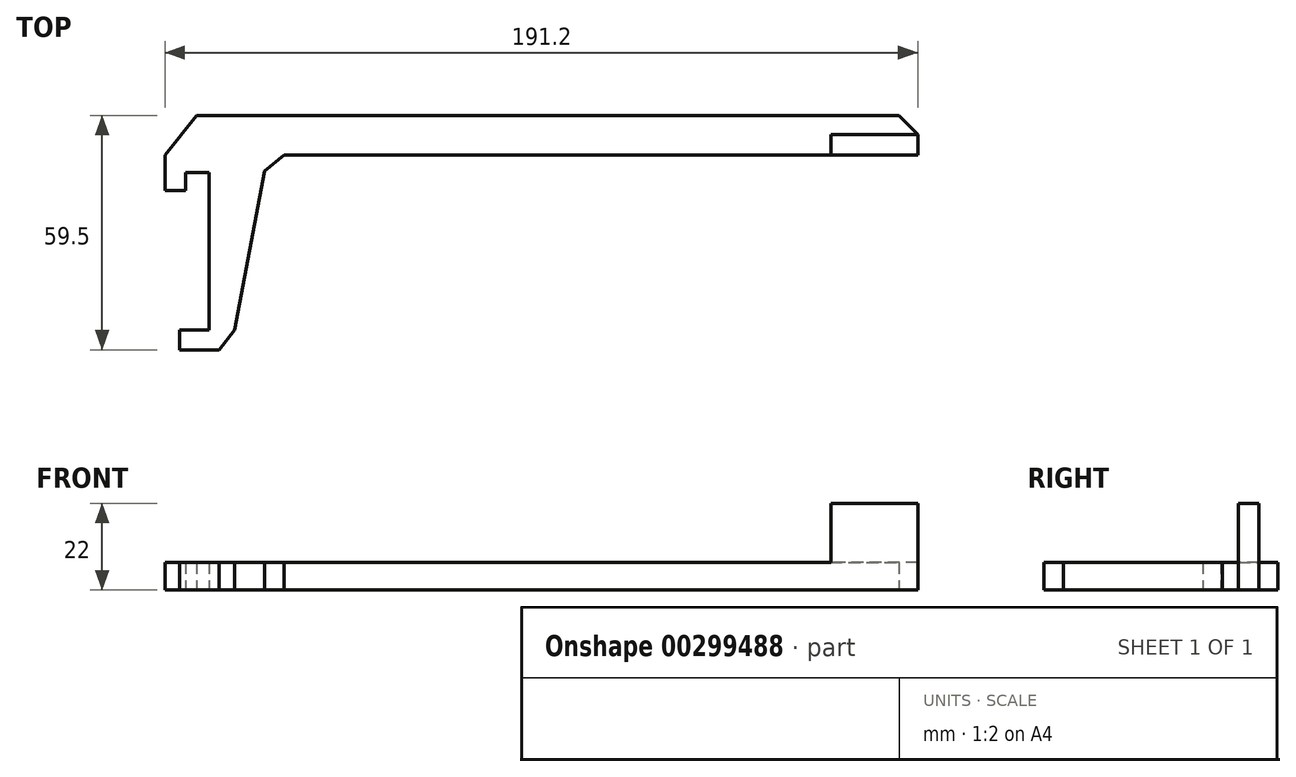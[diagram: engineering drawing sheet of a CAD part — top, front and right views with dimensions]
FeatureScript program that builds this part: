
annotation { "Feature Type Name" : "Feature", "Feature Type Description" : "" }
export const myFeature = defineFeature(function(context is Context, id is Id, definition is map)
    precondition{}
    {
        {
            var Q0;
            Q0=qCreatedBy(makeId("Top.planeOp"),FACE);
            var sketch = newSketch(context, id + "F0", { "sketchPlane" : qUnion([Q0])});
            skLineSegment(sketch, "E0", {"start": v(-18.72, 27.02) * mm, "end": v(-12.72, 27.02) * mm});
            skLineSegment(sketch, "E1", {"start": v(-12.72, 27.02) * mm, "end": v(-12.72, -12.98) * mm});
            skLineSegment(sketch, "E2", {"start": v(-12.72, -12.98) * mm, "end": v(-20.22, -12.98) * mm});
            skLineSegment(sketch, "E3", {"start": v(-20.22, -12.98) * mm, "end": v(-20.22, -17.98) * mm});
            skLineSegment(sketch, "E4", {"start": v(-20.22, -17.98) * mm, "end": v(-10.22, -17.98) * mm});
            skLineSegment(sketch, "E5", {"start": v(-10.22, -17.98) * mm, "end": v(-6.22, -12.98) * mm});
            skLineSegment(sketch, "E6", {"start": v(-18.72, 27.02) * mm, "end": v(-18.72, 22.52) * mm});
            skLineSegment(sketch, "E7", {"start": v(-18.72, 22.52) * mm, "end": v(-23.92, 22.52) * mm});
            skLineSegment(sketch, "E8", {"start": v(-23.92, 22.52) * mm, "end": v(-23.92, 31.52) * mm});
            skLineSegment(sketch, "E9", {"start": v(-21.58, -17.98) * mm, "end": v(-3.78, -17.98) * mm, "construction": true});
            skLineSegment(sketch, "E10", {"start": v(-28.88, 31.52) * mm, "end": v(9.52, 31.52) * mm, "construction": true});
            skLineSegment(sketch, "E11", {"start": v(-23.92, 31.52) * mm, "end": v(-15.92, 41.52) * mm});
            skLineSegment(sketch, "E12", {"start": v(-6.22, -12.98) * mm, "end": v(2.12, 31.52) * mm});
            skLineSegment(sketch, "E13", {"start": v(-12.72, 27.02) * mm, "end": v(1.28, 27.02) * mm, "construction": true});
            skLineSegment(sketch, "E14", {"start": v(-29.11, 41.52) * mm, "end": v(10.02, 41.52) * mm, "construction": true});
            skLineSegment(sketch, "E15", {"start": v(2.12, 31.52) * mm, "end": v(167.28, 31.52) * mm});
            skLineSegment(sketch, "E16", {"start": v(1.36, 27.43) * mm, "end": v(6.28, 31.52) * mm});
            skLineSegment(sketch, "E17", {"start": v(145.28, 31.52) * mm, "end": v(145.28, 36.72) * mm});
            skLineSegment(sketch, "E18", {"start": v(145.28, 36.72) * mm, "end": v(167.28, 36.72) * mm});
            skLineSegment(sketch, "E19", {"start": v(167.28, 36.72) * mm, "end": v(162.48, 41.52) * mm});
            skPoint(sketch, "E20", {"position": v(162.48, 41.52) * mm});
            skLineSegment(sketch, "E21", {"start": v(-15.92, 41.52) * mm, "end": v(162.48, 41.52) * mm});
            skLineSegment(sketch, "E22", {"start": v(167.28, 36.72) * mm, "end": v(167.28, 31.52) * mm});
            skSolve(sketch);
        }
        {
            var Q0;
            Q0 = qSketchRegion(id + "F0", true);
            extrude(context, id + "F1", {"entities" : qUnion([Q0]), "depth" : 7 * mm});
        }
        {
            var Q0;
            {var subQ2=sQuery(id+"F0.wireOp",EDGE,"E17");Q0=makeQuery(id+"F0.imprint","IMPRINT",FACE,{"disambiguationData":[TD([[makeQuery(id+"F0.imprint","IMPRINT",EDGE,{"derivedFrom":subQ2}),-1.0]])]});}
            extrude(context, id + "F2", {"entities" : qUnion([Q0]), "operationType" : NewBodyOperationType.ADD, "depth" : 22 * mm});
        }
    });
